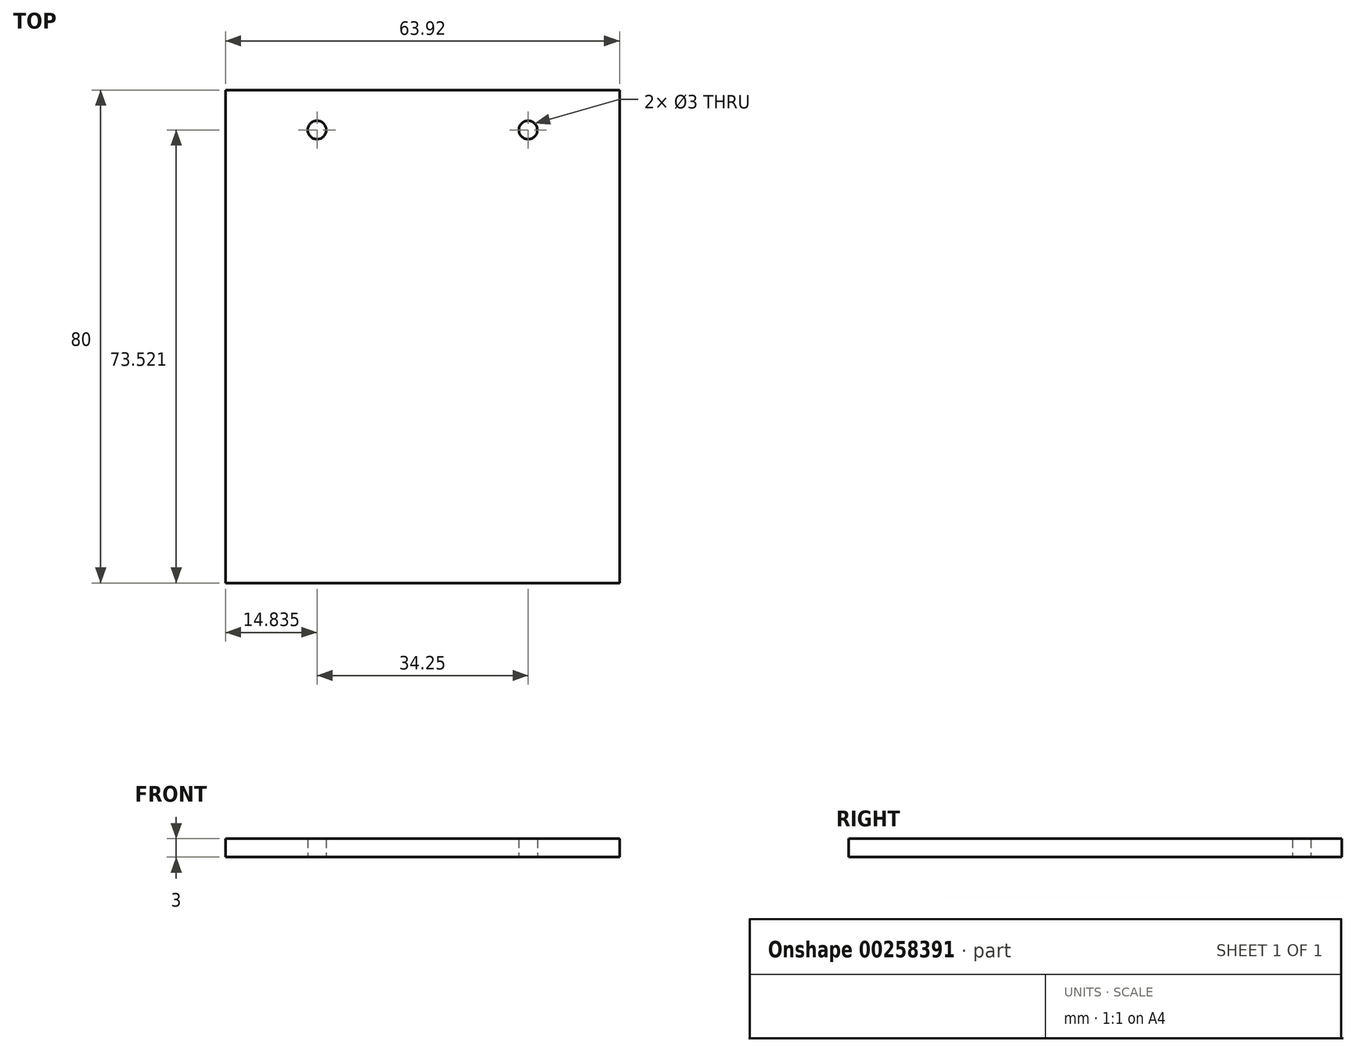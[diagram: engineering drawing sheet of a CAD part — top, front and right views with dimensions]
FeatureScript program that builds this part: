
annotation { "Feature Type Name" : "Feature", "Feature Type Description" : "" }
export const myFeature = defineFeature(function(context is Context, id is Id, definition is map)
    precondition{}
    {
        {
            var Q0;
            Q0=qCreatedBy(makeId("Top.planeOp"),FACE);
            var sketch = newSketch(context, id + "F0", { "sketchPlane" : qUnion([Q0])});
            skLineSegment(sketch, "E0.bottom", {"start": v(31.96, -40) * mm, "end": v(-31.96, -40) * mm});
            skLineSegment(sketch, "E0.top", {"start": v(31.96, 40) * mm, "end": v(-31.96, 40) * mm});
            skLineSegment(sketch, "E0.left", {"start": v(31.96, -40) * mm, "end": v(31.96, 40) * mm});
            skLineSegment(sketch, "E0.right", {"start": v(-31.96, -40) * mm, "end": v(-31.96, 40) * mm});
            skPoint(sketch, "E0.middle", {"position": v(0, 0) * mm});
            skLineSegment(sketch, "E1", {"start": v(-31.96, 33.52) * mm, "end": v(31.96, 33.52) * mm, "construction": true});
            skCircle(sketch, "E2", {"center": v(-17.12, 33.52) * mm, "radius": 1.5 * mm});
            skCircle(sketch, "E3.MirrorC", {"center": v(17.12, 33.52) * mm, "radius": 1.5 * mm});
            skSolve(sketch);
        }
        {
            var Q0;
            Q0 = qSketchRegion(id + "F0", true);
            extrude(context, id + "F1", {"entities" : qUnion([Q0]), "depth" : 3 * mm});
        }
        {
            var Q0;
            Q0=makeQuery(id+"F1.opExtrude","SWEPT_FACE",FACE,{"disambiguationData":[OSD([sQuery(id+"F0.wireOp",EDGE,"E0.bottom")])]});
            cPlane(context, id + "F2", {"entities" : qUnion([Q0]), "cplaneType" : CPlaneType.OFFSET, "offset" : 61.6 * mm, "oppositeDirection" : true, "width" : 150 * mm, "height" : 150 * mm});
        }
    });
